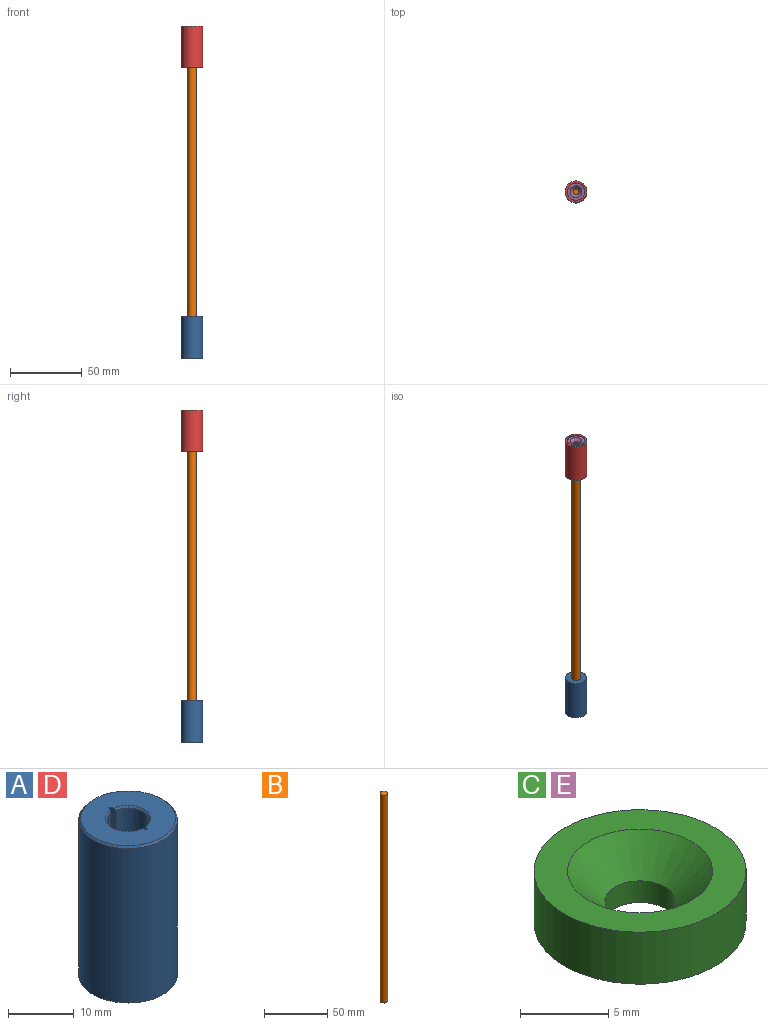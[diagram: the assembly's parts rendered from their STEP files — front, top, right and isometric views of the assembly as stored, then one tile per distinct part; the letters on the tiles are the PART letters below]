
ASSEMBLY  parts=5 mates=4
PART A: 22 faces, bbox 15x15x29 mm
  f0: plane 13.45x12.05mm, normal (0,0,-1), area 98.7mm2, adj f11,f12,f13,f14,f15,f16,f18
  f1: cylinder r=3.15mm len=19.7mm, axis (0,0,-1), area 170.7mm2, adj f2,f7,f10,f19
  f2: plane 20.01x1.07mm, normal (-0.87,0.5,0), area 24.4mm2, adj f1,f3,f8,f10,f19
  f3: plane 20.01x1.07mm, normal (0.87,0.5,0), area 24.4mm2, adj f2,f4,f8,f10,f20
  f4: cylinder r=3.15mm len=19.7mm, axis (0,0,-1), area 170.7mm2, adj f3,f5,f10,f20
  f5: plane 20.01x1.07mm, normal (0.87,-0.5,0), area 24.4mm2, adj f4,f7,f8,f10,f20
  f6: cylinder r=7.5mm len=28.7mm, axis (0,0,-1), area 1352.5mm2, adj f17,f21
  f7: plane 20.01x1.07mm, normal (-0.87,-0.5,0), area 24.4mm2, adj f1,f5,f8,f10,f19
  f8: plane 14.4x14.4mm, normal (0,0,1), area 124.9mm2, adj f2,f3,f5,f7,f19,f20,f21
  f9: cylinder r=1.95mm len=4.7mm, axis (0,0,-1), area 57.6mm2, adj f10,f18
  f10: plane 8.3x6.3mm, normal (0,0,1), area 20.4mm2, adj f1,f2,f3,f4,f5,f7,f9
  f11: cylinder r=6.03mm len=12.02mm, axis (0,0,1), area 72.4mm2, adj f0,f12,f16,f17
  f12: plane 4x0.71mm, normal (-0.87,0.5,0), area 3.3mm2, adj f0,f11,f13,f17
  f13: plane 4x0.71mm, normal (0.87,0.5,0), area 3.3mm2, adj f0,f12,f14,f17
  f14: cylinder r=6.03mm len=12.02mm, axis (0,0,1), area 72.4mm2, adj f0,f13,f15,f17
  f15: plane 4x0.71mm, normal (0.87,-0.5,0), area 3.3mm2, adj f0,f14,f16,f17
  f16: plane 4x0.71mm, normal (-0.87,-0.5,0), area 3.3mm2, adj f0,f11,f15,f17
  f17: plane 15x15mm, normal (0,0,-1), area 62.1mm2, adj f6,f11,f12,f13,f14,f15,f16
  f18: cone r=2.25mm half-angle=45deg, axis (0,0,-1), area 5.6mm2, adj f0,f9
  f19: cone r=3.15mm half-angle=45deg, axis (0,0,1), area 4mm2, adj f1,f2,f7,f8
  f20: cone r=3.15mm half-angle=45deg, axis (0,0,1), area 4mm2, adj f3,f4,f5,f8
  f21: cone r=7.2mm half-angle=45deg, axis (0,0,-1), area 19.6mm2, adj f6,f8
PART B: 3 faces, bbox 6x6x201 mm
  f0: cylinder r=3mm len=201mm, axis (0,0,-1), area 3788.8mm2, adj f1,f2
  f1: plane 6x6mm, normal (0,0,1), area 28.3mm2, adj f0
  f2: plane 6x6mm, normal (0,0,-1), area 28.3mm2, adj f0
PART C: 5 faces, bbox 12x12x3.6 mm
  f0: cylinder r=2mm len=4mm, axis (0,0,-1), area 18.8mm2, adj f3,f4
  f1: cylinder r=6mm len=12mm, axis (0,0,-1), area 135.7mm2, adj f2,f3
  f2: plane 12x12mm, normal (0,0,1), area 60.3mm2, adj f1,f4
  f3: plane 12x12mm, normal (0,0,-1), area 100.5mm2, adj f0,f1
  f4: cone r=2mm half-angle=45deg, axis (0,0,1), area 56.9mm2, adj f0,f2
PART D: same geometry as A
PART E: same geometry as C
PLACE A t=(0,0,-110.9)mm
PLACE B t=(0,0,-100)mm fixed
PLACE C rot(axis=(1,0,0),180deg) t=(0,0,-110.9)mm
PLACE D rot(axis=(1,0,0),180deg) t=(0,0,111.9)mm
PLACE E t=(0,0,111.9)mm
MATE fastened C.f0 <-> A.f1  axis (0,0,1) through (0,0,-110.9)mm
MATE fastened E.f0 <-> D.f1  axis (0,0,-1) through (0,0,111.9)mm
MATE fastened B.f0 <-> D.f1  axis (0,0,1) through (0,0,101)mm
MATE fastened A.f1 <-> B.f0  axis (0,0,1) through (0,0,-105.9)mm
